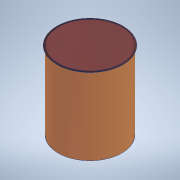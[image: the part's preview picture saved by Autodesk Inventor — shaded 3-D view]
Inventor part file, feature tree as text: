
AUTODESK INVENTOR PART (.ipt)
format: ipt  version: 2021 (Build 250183000, 183)  size: 119,296 bytes
history: native  units: mm
features: thicken_offset x1, sketch x1, other x1, revolve x1
ambient origin geometry x8: Origin, YZ Plane, XZ Plane, XY Plane, X Axis, Y Axis, Z Axis, Center Point
bodies: Solid1 (feature_tree)
feature tree (4):
  thicken_offset  "Thicken1"
  sketch  "Sketch1"  dims[d0=620.0mm d1=255.0mm d2=10.0mm d3=90.0deg d4=2.0mm d5=2.0mm]
  other  "Srf1"
  revolve  "RevolutionSrf1"  [1 undecoded]
note: 1 required parameter value undecoded (feature->parameter linkage not recoverable at this tier; creation-order binding heuristic only, values carry confidence <= 0.55)
